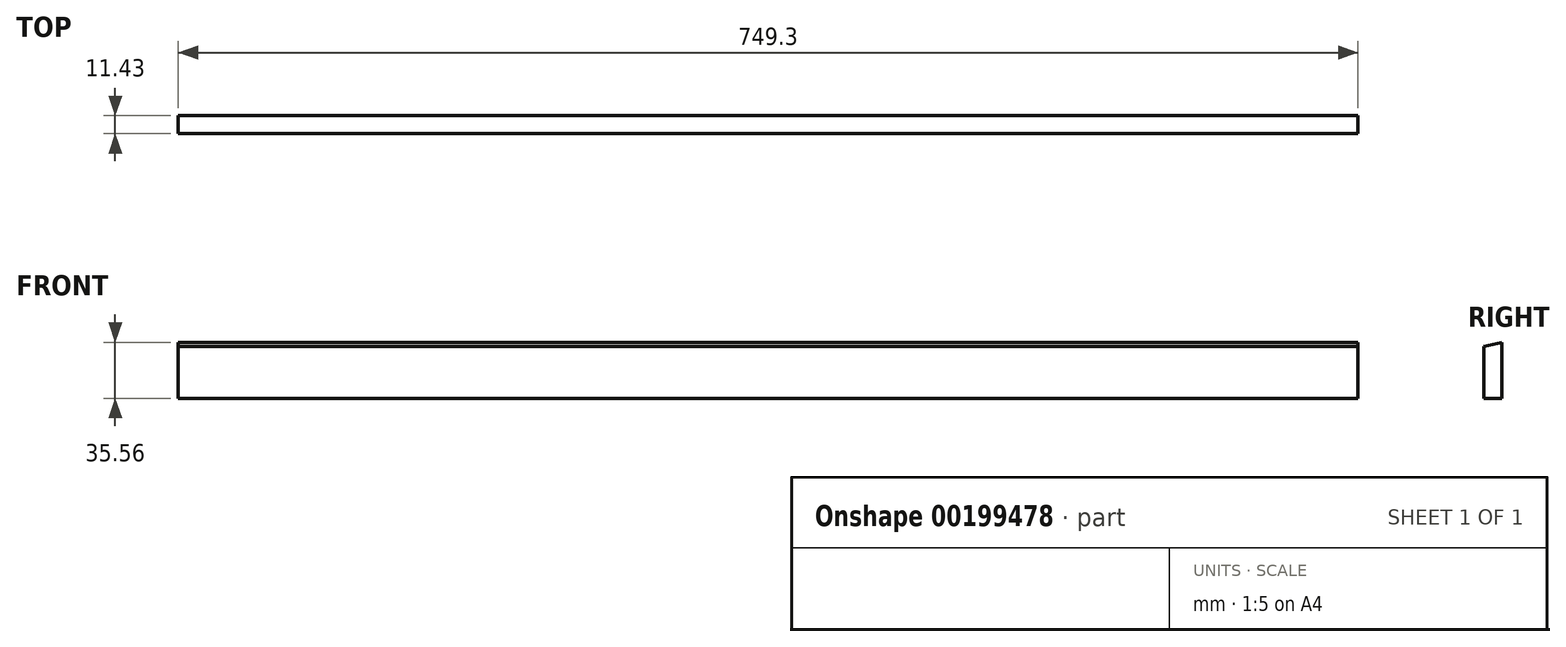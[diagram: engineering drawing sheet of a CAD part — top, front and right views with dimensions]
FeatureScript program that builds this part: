
annotation { "Feature Type Name" : "Feature", "Feature Type Description" : "" }
export const myFeature = defineFeature(function(context is Context, id is Id, definition is map)
    precondition{}
    {
        {
            var Q0;
            Q0=qCreatedBy(makeId("Right.planeOp"),FACE);
            var sketch = newSketch(context, id + "F0", { "sketchPlane" : qUnion([Q0])});
            skLineSegment(sketch, "E0", {"start": v(-61.21, 0) * mm, "end": v(-61.21, 33.02) * mm});
            skLineSegment(sketch, "E1", {"start": v(-61.21, 33.02) * mm, "end": v(-49.78, 35.56) * mm});
            skLineSegment(sketch, "E2", {"start": v(-49.78, 35.56) * mm, "end": v(-49.78, 0) * mm});
            skLineSegment(sketch, "E3", {"start": v(-49.78, 0) * mm, "end": v(-61.21, 0) * mm});
            skSolve(sketch);
        }
        {
            var Q0;
            Q0 = qSketchRegion(id + "F0", true);
            extrude(context, id + "F1", {"entities" : qUnion([Q0]), "depth" : 749.3 * mm});
        }
    });
